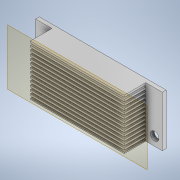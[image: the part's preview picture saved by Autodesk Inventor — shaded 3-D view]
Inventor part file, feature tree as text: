
AUTODESK INVENTOR PART (.ipt)
format: ipt  version: 2021 (Build 250183000, 183)  size: 321,536 bytes
history: native  units: in
note: dims shown in document units (in); Inventor stores cm internally (conversion verified against a paired STEP export)
features: sketch x4, extrude x3, pattern_linear x1, plane x1, hole x1, mirror x1, projected_geometry x1
ambient origin geometry x8: Origin, YZ Plane, XZ Plane, XY Plane, X Axis, Y Axis, Z Axis, Center Point
bodies: Solid1 (feature_tree)
feature tree (12):
  extrude  "Extrusion1"  Depth=1.5748in
  extrude  "Extrusion2"  Depth=0.0591in
  pattern_linear  "Rectangular Pattern1"  Count1=13 Spacing1=0.1181in
  plane  "Work Plane1"
  hole  "Hole2"  [1 undecoded]
  extrude  "Extrusion3"  Depth=0.2362in
  mirror  "Mirror1"
  sketch  "Sketch1"  dims[d0=3.937in d1=1.5748in]
  sketch  "Sketch2"  dims[d2=0.7874in d3=0.0in d4=0.0591in]
  projected_geometry  "Projected Loop1"
  sketch  "Sketch4"  dims[d6=0.0591in]
  sketch  "Sketch5"  dims[d7=0.6693in d8=0.0in d9=5.1181in d11=0.1181in d21=0.7874in d22=0.2362in d23=0.266in d24=0.2362in d25=0.4375in d26=0.6693in d27=0.5635in d28=0.12in d29=0.0in d30=0.2756in d31=0.2756in d32=0.2362in d33=0.5118in d34=0.3937in d35=0.0in]
note: 1 required parameter value undecoded (feature->parameter linkage not recoverable at this tier; creation-order binding heuristic only, values carry confidence <= 0.55)
